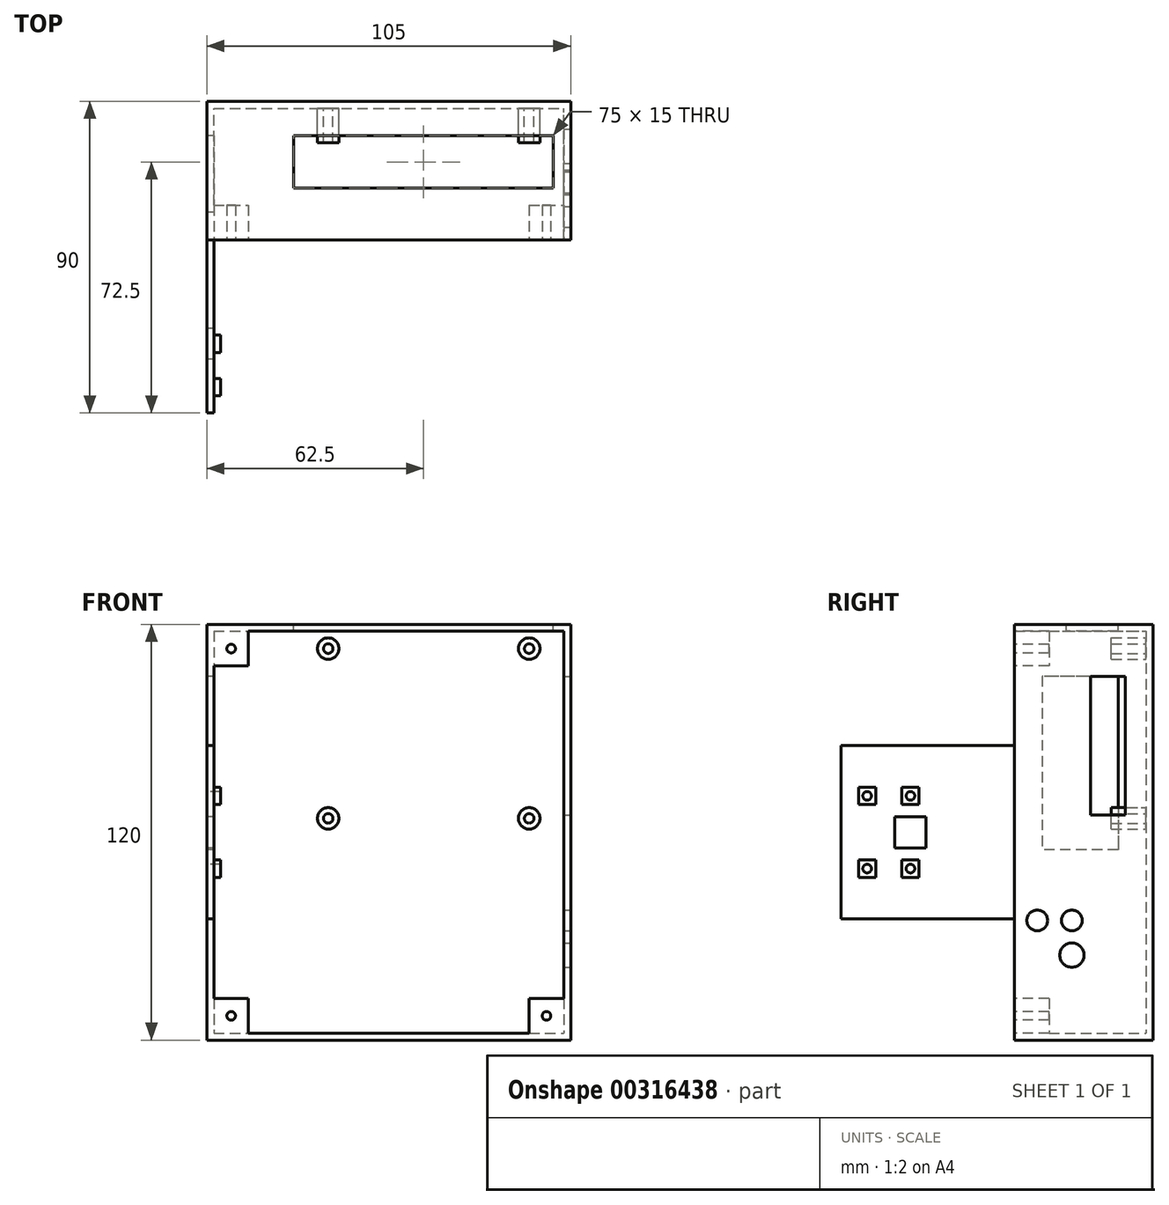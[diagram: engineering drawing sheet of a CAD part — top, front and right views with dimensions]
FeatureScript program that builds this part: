
annotation { "Feature Type Name" : "Feature", "Feature Type Description" : "" }
export const myFeature = defineFeature(function(context is Context, id is Id, definition is map)
    precondition{}
    {
        {
            var Q0;
            Q0=qCreatedBy(makeId("Front.planeOp"),FACE);
            var sketch = newSketch(context, id + "F0", { "sketchPlane" : qUnion([Q0])});
            skLineSegment(sketch, "E0.bottom", {"start": v(-48.56, 66.87) * mm, "end": v(56.44, 66.87) * mm});
            skLineSegment(sketch, "E0.top", {"start": v(-48.56, -53.13) * mm, "end": v(56.44, -53.13) * mm});
            skLineSegment(sketch, "E0.left", {"start": v(-48.56, 66.87) * mm, "end": v(-48.56, -53.13) * mm});
            skLineSegment(sketch, "E0.right", {"start": v(56.44, 66.87) * mm, "end": v(56.44, -53.13) * mm});
            skLineSegment(sketch, "E1.bottom", {"start": v(49.44, 64.87) * mm, "end": v(39.44, 64.87) * mm});
            skLineSegment(sketch, "E1.top", {"start": v(49.44, 54.87) * mm, "end": v(39.44, 54.87) * mm});
            skLineSegment(sketch, "E1.left", {"start": v(49.44, 64.87) * mm, "end": v(49.44, 54.87) * mm});
            skLineSegment(sketch, "E1.right", {"start": v(39.44, 64.87) * mm, "end": v(39.44, 54.87) * mm});
            skLineSegment(sketch, "E2.MirrorCS", {"start": v(-8.56, 64.87) * mm, "end": v(-8.56, 54.87) * mm});
            skLineSegment(sketch, "E3.MirrorCS", {"start": v(-18.56, 64.87) * mm, "end": v(-18.56, 54.87) * mm});
            skLineSegment(sketch, "E4.MirrorCS", {"start": v(-18.56, 54.87) * mm, "end": v(-8.56, 54.87) * mm});
            skLineSegment(sketch, "E5.MirrorCS", {"start": v(-18.56, 64.87) * mm, "end": v(-8.56, 64.87) * mm});
            skLineSegment(sketch, "E6.MirrorCS", {"start": v(-18.56, 5.87) * mm, "end": v(-18.56, 15.87) * mm});
            skLineSegment(sketch, "E7.MirrorCS", {"start": v(-8.56, 5.87) * mm, "end": v(-8.56, 15.87) * mm});
            skLineSegment(sketch, "E8.MirrorCS", {"start": v(-18.56, 15.87) * mm, "end": v(-8.56, 15.87) * mm});
            skLineSegment(sketch, "E9.MirrorCS", {"start": v(-18.56, 5.87) * mm, "end": v(-8.56, 5.87) * mm});
            skLineSegment(sketch, "E10.MirrorCS", {"start": v(39.44, 5.87) * mm, "end": v(39.44, 15.87) * mm});
            skLineSegment(sketch, "E11.MirrorCS", {"start": v(49.44, 5.87) * mm, "end": v(49.44, 15.87) * mm});
            skLineSegment(sketch, "E12.MirrorCS", {"start": v(49.44, 15.87) * mm, "end": v(39.44, 15.87) * mm});
            skLineSegment(sketch, "E13.MirrorCS", {"start": v(49.44, 5.87) * mm, "end": v(39.44, 5.87) * mm});
            skPoint(sketch, "E14.centerSnap0", {"position": v(39.44, 59.87) * mm});
            skPoint(sketch, "E14.centerSnap1", {"position": v(44.44, 64.87) * mm});
            skPoint(sketch, "E15.centerSnap0", {"position": v(39.44, 10.87) * mm});
            skPoint(sketch, "E15.centerSnap1", {"position": v(44.44, 15.87) * mm});
            skPoint(sketch, "E16.centerSnap0", {"position": v(-18.56, 10.87) * mm});
            skPoint(sketch, "E16.centerSnap1", {"position": v(-13.56, 15.87) * mm});
            skPoint(sketch, "E17.centerSnap0", {"position": v(-18.56, 59.87) * mm});
            skPoint(sketch, "E17.centerSnap1", {"position": v(-13.56, 64.87) * mm});
            skSolve(sketch);
        }
        {
            var Q0;
            Q0=makeQuery(id+"F0.imprint","IMPRINT",FACE,{"disambiguationData":[TD([[makeQuery(id+"F0.imprint","IMPRINT",EDGE,{"derivedFrom":sQuery(id+"F0.wireOp",EDGE,"E0.bottom")}),-1.0]])]});
            var Q1;
            Q1=makeQuery(id+"F0.imprint","IMPRINT",FACE,{"disambiguationData":[TD([[makeQuery(id+"F0.imprint","IMPRINT",EDGE,{"derivedFrom":sQuery(id+"F0.wireOp",EDGE,"E2.MirrorCS")}),-1.0]])]});
            var Q2;
            Q2=makeQuery(id+"F0.imprint","IMPRINT",FACE,{"disambiguationData":[TD([[makeQuery(id+"F0.imprint","IMPRINT",EDGE,{"derivedFrom":sQuery(id+"F0.wireOp",EDGE,"E6.MirrorCS")}),-1.0]])]});
            var Q3;
            Q3=makeQuery(id+"F0.imprint","IMPRINT",FACE,{"disambiguationData":[TD([[makeQuery(id+"F0.imprint","IMPRINT",EDGE,{"derivedFrom":sQuery(id+"F0.wireOp",EDGE,"E10.MirrorCS")}),-1.0]])]});
            var Q4;
            Q4=makeQuery(id+"F0.imprint","IMPRINT",FACE,{"disambiguationData":[TD([[makeQuery(id+"F0.imprint","IMPRINT",EDGE,{"derivedFrom":sQuery(id+"F0.wireOp",EDGE,"E1.bottom")}),1.0]])]});
            extrude(context, id + "F1", {"entities" : qUnion([Q0, Q1, Q2, Q3, Q4]), "depth" : 40 * mm});
        }
        {
            var Q0;
            Q0=makeQuery(id+"F1.opExtrude","CAP_FACE",FACE,{"disambiguationData":[OSD([sQuery(id+"F0.wireOp",EDGE,"E0.bottom"),sQuery(id+"F0.wireOp",EDGE,"E0.top"),sQuery(id+"F0.wireOp",EDGE,"E0.left"),sQuery(id+"F0.wireOp",EDGE,"E0.right"),sQuery(id+"F0.wireOp",EDGE,"E14"),sQuery(id+"F0.wireOp",EDGE,"E15"),sQuery(id+"F0.wireOp",EDGE,"E16"),sQuery(id+"F0.wireOp",EDGE,"E17")])],"isStart":false});
            shell(context, id + "F2", {"entities" : qUnion([Q0]), "thickness" : 2 * mm});
        }
        {
            var Q0;
            Q0=makeQuery(id+"F0.imprint","IMPRINT",FACE,{"disambiguationData":[TD([[makeQuery(id+"F0.imprint","IMPRINT",EDGE,{"derivedFrom":sQuery(id+"F0.wireOp",EDGE,"E1.bottom")}),1.0]])]});
            var sketch = newSketch(context, id + "F3", { "sketchPlane" : qUnion([Q0])});
            skCircle(sketch, "E18", {"center": v(44.44, 59.87) * mm, "radius": 1.38 * mm});
            skPoint(sketch, "E18.centerSnap0", {"position": v(39.44, 59.87) * mm});
            skPoint(sketch, "E18.centerSnap1", {"position": v(44.44, 64.87) * mm});
            skCircle(sketch, "E19", {"center": v(44.44, 10.87) * mm, "radius": 1.38 * mm});
            skPoint(sketch, "E19.centerSnap0", {"position": v(39.44, 10.87) * mm});
            skPoint(sketch, "E19.centerSnap1", {"position": v(44.44, 15.87) * mm});
            skCircle(sketch, "E20", {"center": v(-13.56, 10.87) * mm, "radius": 1.38 * mm});
            skPoint(sketch, "E20.centerSnap0", {"position": v(-18.56, 10.87) * mm});
            skPoint(sketch, "E20.centerSnap1", {"position": v(-13.56, 15.87) * mm});
            skCircle(sketch, "E21", {"center": v(-13.56, 59.87) * mm, "radius": 1.38 * mm});
            skLineSegment(sketch, "E22.0.0", {"start": v(-46.56, 64.87) * mm, "end": v(-46.56, -51.13) * mm});
            skLineSegment(sketch, "E22.0.1", {"start": v(-46.56, -51.13) * mm, "end": v(54.44, -51.13) * mm});
            skLineSegment(sketch, "E22.0.2", {"start": v(54.44, -51.13) * mm, "end": v(54.44, 64.87) * mm});
            skLineSegment(sketch, "E22.0.3", {"start": v(54.44, 64.87) * mm, "end": v(-46.56, 64.87) * mm});
            skSolve(sketch);
        }
        {
            var Q0;
            Q0=makeQuery(id+"F1.opExtrude","CAP_FACE",FACE,{"disambiguationData":[OSD([sQuery(id+"F0.wireOp",EDGE,"E0.bottom"),sQuery(id+"F0.wireOp",EDGE,"E0.top"),sQuery(id+"F0.wireOp",EDGE,"E0.left"),sQuery(id+"F0.wireOp",EDGE,"E0.right"),sQuery(id+"F0.wireOp",EDGE,"E14"),sQuery(id+"F0.wireOp",EDGE,"E15"),sQuery(id+"F0.wireOp",EDGE,"E16"),sQuery(id+"F0.wireOp",EDGE,"E17")])],"isStart":false});
            var sketch = newSketch(context, id + "F4", { "sketchPlane" : qUnion([Q0])});
            skLineSegment(sketch, "E23.bottom", {"start": v(-48.56, 31.87) * mm, "end": v(-46.56, 31.87) * mm});
            skLineSegment(sketch, "E23.top", {"start": v(-48.56, -18.13) * mm, "end": v(-46.56, -18.13) * mm});
            skLineSegment(sketch, "E23.left", {"start": v(-48.56, 31.87) * mm, "end": v(-48.56, -18.13) * mm});
            skLineSegment(sketch, "E23.right", {"start": v(-46.56, 31.87) * mm, "end": v(-46.56, -18.13) * mm});
            skSolve(sketch);
        }
        {
            var Q0;
            Q0=makeQuery(id+"F4.imprint","IMPRINT",FACE,{"disambiguationData":[TD([[makeQuery(id+"F4.imprint","IMPRINT",EDGE,{"derivedFrom":sQuery(id+"F4.wireOp",EDGE,"E23.bottom")}),-1.0]])]});
            extrude(context, id + "F5", {"entities" : qUnion([Q0]), "operationType" : NewBodyOperationType.ADD, "depth" : 50 * mm});
        }
        {
            var Q0;
            Q0=makeQuery(id+"F5.boolean.opBoolean","MERGE",FACE,{"derivedFrom":[makeQuery(id+"F1.opExtrude","SWEPT_FACE",FACE,{"disambiguationData":[OSD([sQuery(id+"F0.wireOp",EDGE,"E0.left")])]}),makeQuery(id+"F5.opExtrude","SWEPT_FACE",FACE,{"disambiguationData":[OSD([sQuery(id+"F4.wireOp",EDGE,"E23.left")])]})]});
            var sketch = newSketch(context, id + "F6", { "sketchPlane" : qUnion([Q0])});
            skLineSegment(sketch, "E24.bottom", {"start": v(74.5, 2.37) * mm, "end": v(65.5, 2.37) * mm});
            skLineSegment(sketch, "E24.top", {"start": v(74.5, 11.37) * mm, "end": v(65.5, 11.37) * mm});
            skLineSegment(sketch, "E24.left", {"start": v(74.5, 2.37) * mm, "end": v(74.5, 11.37) * mm});
            skLineSegment(sketch, "E24.right", {"start": v(65.5, 2.37) * mm, "end": v(65.5, 11.37) * mm});
            skPoint(sketch, "E25.startSnap0", {"position": v(70, 11.37) * mm});
            skPoint(sketch, "E25.endSnap0", {"position": v(70, 2.37) * mm});
            skCircle(sketch, "E26", {"center": v(70, -3.63) * mm, "radius": 1.25 * mm});
            skCircle(sketch, "E27", {"center": v(70, 17.37) * mm, "radius": 1.25 * mm});
            skCircle(sketch, "E28", {"center": v(82.5, -3.63) * mm, "radius": 1.25 * mm});
            skCircle(sketch, "E29", {"center": v(82.5, 17.37) * mm, "radius": 1.25 * mm});
            skSolve(sketch);
        }
        {
            var Q0;
            Q0=makeQuery(id+"F6.imprint","IMPRINT",FACE,{"disambiguationData":[TD([[makeQuery(id+"F6.imprint","IMPRINT",EDGE,{"derivedFrom":sQuery(id+"F6.wireOp",EDGE,"E26")}),1.0]])]});
            var Q1;
            Q1=makeQuery(id+"F6.imprint","IMPRINT",FACE,{"disambiguationData":[TD([[makeQuery(id+"F6.imprint","IMPRINT",EDGE,{"derivedFrom":sQuery(id+"F6.wireOp",EDGE,"E27")}),1.0]])]});
            var Q2;
            Q2=makeQuery(id+"F6.imprint","IMPRINT",FACE,{"disambiguationData":[TD([[makeQuery(id+"F6.imprint","IMPRINT",EDGE,{"derivedFrom":sQuery(id+"F6.wireOp",EDGE,"E28")}),1.0]])]});
            var Q3;
            Q3=makeQuery(id+"F6.imprint","IMPRINT",FACE,{"disambiguationData":[TD([[makeQuery(id+"F6.imprint","IMPRINT",EDGE,{"derivedFrom":sQuery(id+"F6.wireOp",EDGE,"E29")}),1.0]])]});
            var Q4;
            Q4=makeQuery(id+"F6.imprint","IMPRINT",FACE,{"disambiguationData":[TD([[makeQuery(id+"F6.imprint","IMPRINT",EDGE,{"derivedFrom":sQuery(id+"F6.wireOp",EDGE,"E24.bottom")}),-1.0]])]});
            extrude(context, id + "F7", {"entities" : qUnion([Q0, Q1, Q2, Q3, Q4]), "operationType" : NewBodyOperationType.REMOVE, "oppositeDirection" : true, "depth" : 2 * mm});
        }
        {
            var Q0;
            Q0=makeQuery(id+"F5.boolean.opBoolean","MERGE",FACE,{"derivedFrom":[makeQuery(id+"F2.opShell","OFFSET_FACE",FACE,{"disambiguationData":[OSD([sQuery(id+"F0.wireOp",EDGE,"E0.left")])]}),makeQuery(id+"F5.opExtrude","SWEPT_FACE",FACE,{"disambiguationData":[OSD([sQuery(id+"F4.wireOp",EDGE,"E23.right")])]})]});
            var sketch = newSketch(context, id + "F8", { "sketchPlane" : qUnion([Q0])});
            skLineSegment(sketch, "E30.bottom", {"start": v(-80, 19.87) * mm, "end": v(-85, 19.87) * mm});
            skLineSegment(sketch, "E30.top", {"start": v(-80, 14.87) * mm, "end": v(-85, 14.87) * mm});
            skLineSegment(sketch, "E30.left", {"start": v(-80, 19.87) * mm, "end": v(-80, 14.87) * mm});
            skLineSegment(sketch, "E30.right", {"start": v(-85, 19.87) * mm, "end": v(-85, 14.87) * mm});
            skPoint(sketch, "E30.middle", {"position": v(-82.5, 17.37) * mm});
            skLineSegment(sketch, "E31.bottom", {"start": v(-72.5, 19.87) * mm, "end": v(-67.5, 19.87) * mm});
            skLineSegment(sketch, "E31.top", {"start": v(-72.5, 14.87) * mm, "end": v(-67.5, 14.87) * mm});
            skLineSegment(sketch, "E31.left", {"start": v(-72.5, 19.87) * mm, "end": v(-72.5, 14.87) * mm});
            skLineSegment(sketch, "E31.right", {"start": v(-67.5, 19.87) * mm, "end": v(-67.5, 14.87) * mm});
            skPoint(sketch, "E31.middle", {"position": v(-70, 17.37) * mm});
            skLineSegment(sketch, "E32.bottom", {"start": v(-85, -1.13) * mm, "end": v(-80, -1.13) * mm});
            skLineSegment(sketch, "E32.top", {"start": v(-85, -6.13) * mm, "end": v(-80, -6.13) * mm});
            skLineSegment(sketch, "E32.left", {"start": v(-85, -1.13) * mm, "end": v(-85, -6.13) * mm});
            skLineSegment(sketch, "E32.right", {"start": v(-80, -1.13) * mm, "end": v(-80, -6.13) * mm});
            skPoint(sketch, "E32.middle", {"position": v(-82.5, -3.63) * mm});
            skLineSegment(sketch, "E33.bottom", {"start": v(-72.5, -1.13) * mm, "end": v(-67.5, -1.13) * mm});
            skLineSegment(sketch, "E33.top", {"start": v(-72.5, -6.13) * mm, "end": v(-67.5, -6.13) * mm});
            skLineSegment(sketch, "E33.left", {"start": v(-72.5, -1.13) * mm, "end": v(-72.5, -6.13) * mm});
            skLineSegment(sketch, "E33.right", {"start": v(-67.5, -1.13) * mm, "end": v(-67.5, -6.13) * mm});
            skPoint(sketch, "E33.middle", {"position": v(-70, -3.63) * mm});
            skCircle(sketch, "E34.0", {"center": v(-82.5, 17.37) * mm, "radius": 1.25 * mm});
            skCircle(sketch, "E34.1", {"center": v(-70, 17.37) * mm, "radius": 1.25 * mm});
            skCircle(sketch, "E34.2", {"center": v(-70, -3.63) * mm, "radius": 1.25 * mm});
            skCircle(sketch, "E34.3", {"center": v(-82.5, -3.63) * mm, "radius": 1.25 * mm});
            skSolve(sketch);
        }
        {
            var Q0;
            Q0 = qSketchRegion(id + "F8", true);
            extrude(context, id + "F9", {"entities" : qUnion([Q0]), "operationType" : NewBodyOperationType.ADD, "depth" : 2 * mm});
        }
        {
            var Q0;
            Q0=makeQuery(id+"F1.opExtrude","SWEPT_FACE",FACE,{"disambiguationData":[OSD([sQuery(id+"F0.wireOp",EDGE,"E0.bottom")])]});
            var sketch = newSketch(context, id + "F10", { "sketchPlane" : qUnion([Q0])});
            skLineSegment(sketch, "E35.bottom", {"start": v(51.44, -10) * mm, "end": v(-23.56, -10) * mm});
            skLineSegment(sketch, "E35.top", {"start": v(51.44, -25) * mm, "end": v(-23.56, -25) * mm});
            skLineSegment(sketch, "E35.left", {"start": v(51.44, -10) * mm, "end": v(51.44, -25) * mm});
            skLineSegment(sketch, "E35.right", {"start": v(-23.56, -10) * mm, "end": v(-23.56, -25) * mm});
            skSolve(sketch);
        }
        {
            var Q0;
            Q0 = qSketchRegion(id + "F10", true);
            extrude(context, id + "F11", {"entities" : qUnion([Q0]), "operationType" : NewBodyOperationType.REMOVE, "oppositeDirection" : true, "depth" : 2 * mm});
        }
        {
            var Q0;
            Q0=makeQuery(id+"F5.boolean.opBoolean","MERGE",FACE,{"derivedFrom":[makeQuery(id+"F1.opExtrude","SWEPT_FACE",FACE,{"disambiguationData":[OSD([sQuery(id+"F0.wireOp",EDGE,"E0.left")])]}),makeQuery(id+"F5.opExtrude","SWEPT_FACE",FACE,{"disambiguationData":[OSD([sQuery(id+"F4.wireOp",EDGE,"E23.left")])]})]});
            var sketch = newSketch(context, id + "F12", { "sketchPlane" : qUnion([Q0])});
            skLineSegment(sketch, "E36.bottom", {"start": v(10, 51.87) * mm, "end": v(32, 51.87) * mm});
            skLineSegment(sketch, "E36.top", {"start": v(10, 1.87) * mm, "end": v(32, 1.87) * mm});
            skLineSegment(sketch, "E36.left", {"start": v(10, 51.87) * mm, "end": v(10, 1.87) * mm});
            skLineSegment(sketch, "E36.right", {"start": v(32, 51.87) * mm, "end": v(32, 1.87) * mm});
            skSolve(sketch);
        }
        {
            var Q0;
            Q0 = qSketchRegion(id + "F12", true);
            extrude(context, id + "F13", {"entities" : qUnion([Q0]), "operationType" : NewBodyOperationType.REMOVE, "oppositeDirection" : true, "depth" : 2 * mm});
        }
        {
            var Q0;
            Q0=makeQuery(id+"F2.opShell","OFFSET_FACE",FACE,{"disambiguationData":[OSD([sQuery(id+"F0.wireOp",EDGE,"E0.bottom"),sQuery(id+"F0.wireOp",EDGE,"E0.top"),sQuery(id+"F0.wireOp",EDGE,"E0.left"),sQuery(id+"F0.wireOp",EDGE,"E0.right")])]});
            var sketch = newSketch(context, id + "F14", { "sketchPlane" : qUnion([Q0])});
            skCircle(sketch, "E37", {"center": v(-13.56, 59.87) * mm, "radius": 3.1 * mm});
            skCircle(sketch, "E38", {"center": v(44.44, 59.87) * mm, "radius": 3.1 * mm});
            skCircle(sketch, "E39", {"center": v(-13.56, 10.87) * mm, "radius": 3.1 * mm});
            skCircle(sketch, "E40", {"center": v(44.44, 10.87) * mm, "radius": 3.1 * mm});
            skCircle(sketch, "E41.0", {"center": v(-13.56, 59.87) * mm, "radius": 1.38 * mm});
            skCircle(sketch, "E42.0", {"center": v(-13.56, 10.87) * mm, "radius": 1.38 * mm});
            skCircle(sketch, "E43.0", {"center": v(44.44, 10.87) * mm, "radius": 1.38 * mm});
            skCircle(sketch, "E44.0", {"center": v(44.44, 59.87) * mm, "radius": 1.38 * mm});
            skSolve(sketch);
        }
        {
            var Q0;
            Q0=makeQuery(id+"F14.imprint","IMPRINT",FACE,{"disambiguationData":[TD([[makeQuery(id+"F14.imprint","IMPRINT",EDGE,{"derivedFrom":sQuery(id+"F14.wireOp",EDGE,"E37")}),1.0]])]});
            var Q1;
            Q1=makeQuery(id+"F14.imprint","IMPRINT",FACE,{"disambiguationData":[TD([[makeQuery(id+"F14.imprint","IMPRINT",EDGE,{"derivedFrom":sQuery(id+"F14.wireOp",EDGE,"E38")}),1.0]])]});
            var Q2;
            Q2=makeQuery(id+"F14.imprint","IMPRINT",FACE,{"disambiguationData":[TD([[makeQuery(id+"F14.imprint","IMPRINT",EDGE,{"derivedFrom":sQuery(id+"F14.wireOp",EDGE,"E40")}),1.0]])]});
            var Q3;
            Q3=makeQuery(id+"F14.imprint","IMPRINT",FACE,{"disambiguationData":[TD([[makeQuery(id+"F14.imprint","IMPRINT",EDGE,{"derivedFrom":sQuery(id+"F14.wireOp",EDGE,"E39")}),1.0]])]});
            extrude(context, id + "F15", {"entities" : qUnion([Q0, Q1, Q2, Q3]), "operationType" : NewBodyOperationType.ADD, "depth" : 10 * mm});
        }
        {
            var Q0;
            Q0=makeQuery(id+"F1.opExtrude","SWEPT_FACE",FACE,{"disambiguationData":[OSD([sQuery(id+"F0.wireOp",EDGE,"E0.right")])]});
            var sketch = newSketch(context, id + "F16", { "sketchPlane" : qUnion([Q0])});
            skCircle(sketch, "E45", {"center": v(-23.4, -18.6) * mm, "radius": 3 * mm});
            skCircle(sketch, "E46", {"center": v(-23.4, -28.6) * mm, "radius": 3.5 * mm});
            skCircle(sketch, "E47", {"center": v(-33.4, -18.6) * mm, "radius": 3 * mm});
            skLineSegment(sketch, "E48.bottom", {"start": v(-8, 51.87) * mm, "end": v(-18, 51.87) * mm});
            skLineSegment(sketch, "E48.top", {"start": v(-8, 11.87) * mm, "end": v(-18, 11.87) * mm});
            skLineSegment(sketch, "E48.left", {"start": v(-8, 51.87) * mm, "end": v(-8, 11.87) * mm});
            skLineSegment(sketch, "E48.right", {"start": v(-18, 51.87) * mm, "end": v(-18, 11.87) * mm});
            skSolve(sketch);
        }
        {
            var Q0;
            Q0 = qSketchRegion(id + "F16", true);
            extrude(context, id + "F17", {"entities" : qUnion([Q0]), "operationType" : NewBodyOperationType.REMOVE, "oppositeDirection" : true, "depth" : 2 * mm});
        }
        {
            var Q0;
            Q0=makeQuery(id+"F1.opExtrude","CAP_FACE",FACE,{"disambiguationData":[OSD([sQuery(id+"F0.wireOp",EDGE,"E0.bottom"),sQuery(id+"F0.wireOp",EDGE,"E0.top"),sQuery(id+"F0.wireOp",EDGE,"E0.left"),sQuery(id+"F0.wireOp",EDGE,"E0.right")])],"isStart":false});
            var sketch = newSketch(context, id + "F18", { "sketchPlane" : qUnion([Q0])});
            skLineSegment(sketch, "E49.bottom", {"start": v(-46.56, -51.13) * mm, "end": v(-36.56, -51.13) * mm});
            skLineSegment(sketch, "E49.top", {"start": v(-46.56, -41.13) * mm, "end": v(-36.56, -41.13) * mm});
            skLineSegment(sketch, "E49.left", {"start": v(-46.56, -51.13) * mm, "end": v(-46.56, -41.13) * mm});
            skLineSegment(sketch, "E49.right", {"start": v(-36.56, -51.13) * mm, "end": v(-36.56, -41.13) * mm});
            skLineSegment(sketch, "E50.bottom", {"start": v(54.44, -51.13) * mm, "end": v(44.44, -51.13) * mm});
            skLineSegment(sketch, "E50.top", {"start": v(54.44, -41.13) * mm, "end": v(44.44, -41.13) * mm});
            skLineSegment(sketch, "E50.left", {"start": v(54.44, -51.13) * mm, "end": v(54.44, -41.13) * mm});
            skLineSegment(sketch, "E50.right", {"start": v(44.44, -51.13) * mm, "end": v(44.44, -41.13) * mm});
            skLineSegment(sketch, "E51.bottom", {"start": v(-46.56, 64.87) * mm, "end": v(-36.56, 64.87) * mm});
            skLineSegment(sketch, "E51.top", {"start": v(-46.56, 54.87) * mm, "end": v(-36.56, 54.87) * mm});
            skLineSegment(sketch, "E51.left", {"start": v(-46.56, 64.87) * mm, "end": v(-46.56, 54.87) * mm});
            skLineSegment(sketch, "E51.right", {"start": v(-36.56, 64.87) * mm, "end": v(-36.56, 54.87) * mm});
            skCircle(sketch, "E52", {"center": v(-41.56, -46.13) * mm, "radius": 1.25 * mm});
            skPoint(sketch, "E52.centerSnap0", {"position": v(-41.56, -51.13) * mm});
            skPoint(sketch, "E52.centerSnap1", {"position": v(-46.56, -46.13) * mm});
            skCircle(sketch, "E53", {"center": v(49.44, -46.13) * mm, "radius": 1.25 * mm});
            skPoint(sketch, "E53.centerSnap0", {"position": v(49.44, -51.13) * mm});
            skPoint(sketch, "E53.centerSnap1", {"position": v(44.44, -46.13) * mm});
            skCircle(sketch, "E54", {"center": v(-41.56, 59.87) * mm, "radius": 1.25 * mm});
            skPoint(sketch, "E54.centerSnap0", {"position": v(-41.56, 64.87) * mm});
            skPoint(sketch, "E54.centerSnap1", {"position": v(-46.56, 59.87) * mm});
            skSolve(sketch);
        }
        {
            var Q0;
            Q0 = qSketchRegion(id + "F18", true);
            extrude(context, id + "F19", {"entities" : qUnion([Q0]), "operationType" : NewBodyOperationType.ADD, "oppositeDirection" : true, "depth" : 10 * mm, "offsetDistance" : 25 * mm});
        }
    });
